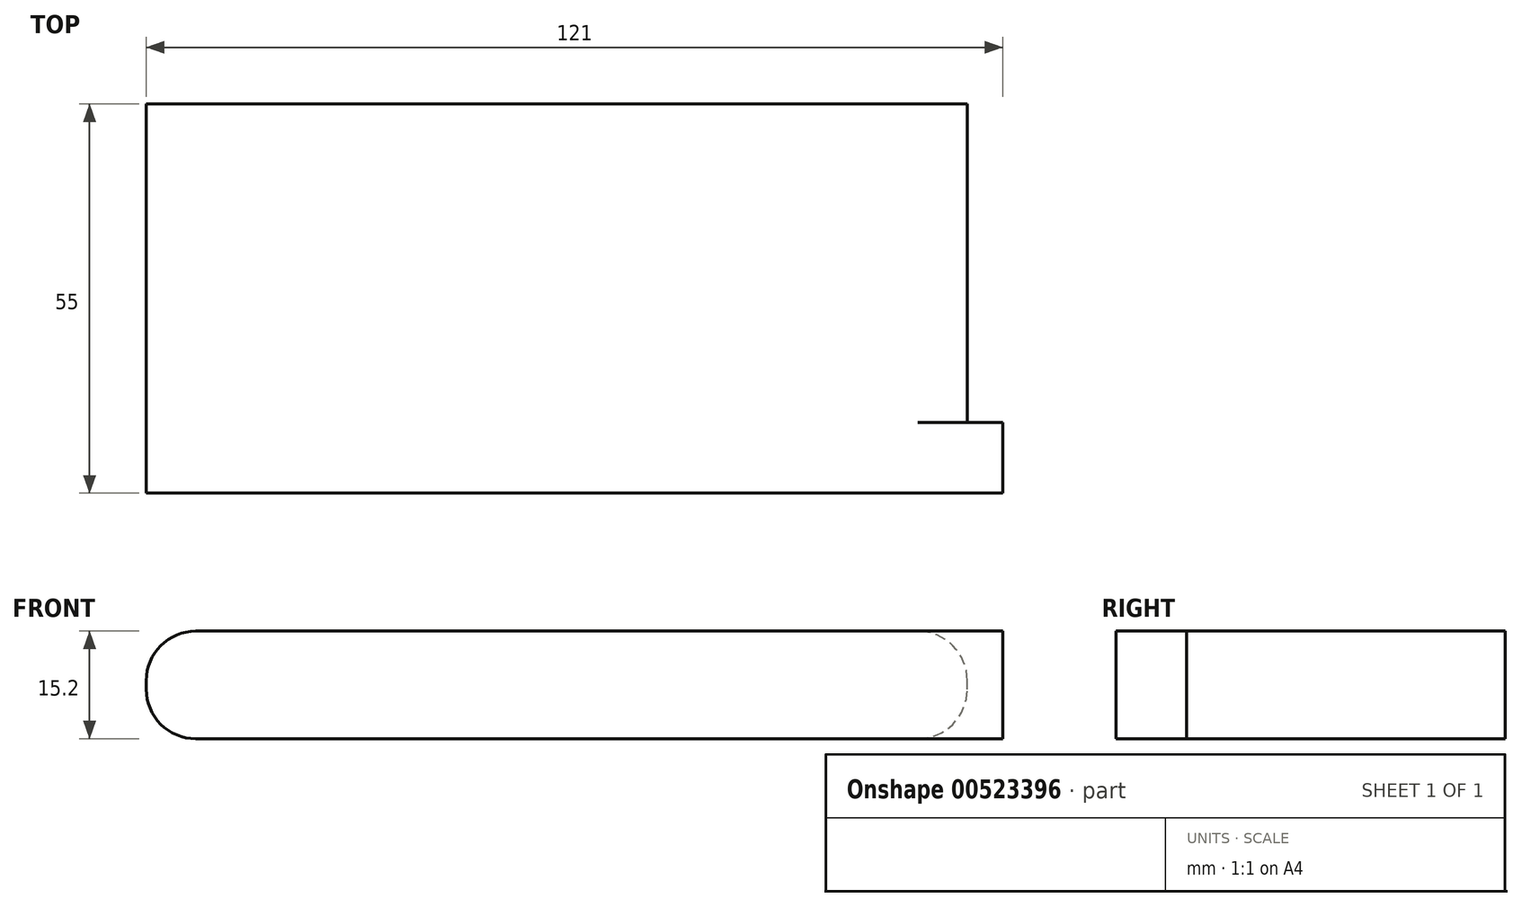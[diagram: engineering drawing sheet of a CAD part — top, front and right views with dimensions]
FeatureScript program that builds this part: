
annotation { "Feature Type Name" : "Feature", "Feature Type Description" : "" }
export const myFeature = defineFeature(function(context is Context, id is Id, definition is map)
    precondition{}
    {
        {
            var Q0;
            Q0=qCreatedBy(makeId("Top.planeOp"),FACE);
            var sketch = newSketch(context, id + "F0", { "sketchPlane" : qUnion([Q0])});
            skLineSegment(sketch, "E0.bottom", {"start": v(58, 27.5) * mm, "end": v(-58, 27.5) * mm});
            skLineSegment(sketch, "E0.top", {"start": v(58, -27.5) * mm, "end": v(-58, -27.5) * mm});
            skLineSegment(sketch, "E0.left", {"start": v(58, 27.5) * mm, "end": v(58, -27.5) * mm});
            skLineSegment(sketch, "E0.right", {"start": v(-58, 27.5) * mm, "end": v(-58, -27.5) * mm});
            skPoint(sketch, "E0.middle", {"position": v(0, 0) * mm});
            skSolve(sketch);
        }
        {
            var Q0;
            Q0=makeQuery(id+"F0.imprint","IMPRINT",FACE,{"disambiguationData":[TD([[makeQuery(id+"F0.imprint","IMPRINT",EDGE,{"derivedFrom":sQuery(id+"F0.wireOp",EDGE,"E0.bottom")}),1.0]])]});
            extrude(context, id + "F1", {"entities" : qUnion([Q0]), "depth" : 15.2 * mm, "offsetDistance" : 25 * mm});
        }
        {
            var Q0;
            Q0=makeQuery(id+"F1.opExtrude","CAP_EDGE",EDGE,{"disambiguationData":[OSD([sQuery(id+"F0.wireOp",EDGE,"E0.left")])],"isStart":false});
            var Q1;
            Q1=makeQuery(id+"F1.opExtrude","CAP_EDGE",EDGE,{"disambiguationData":[OSD([sQuery(id+"F0.wireOp",EDGE,"E0.left")])],"isStart":true});
            var Q2;
            Q2=makeQuery(id+"F1.opExtrude","CAP_EDGE",EDGE,{"disambiguationData":[OSD([sQuery(id+"F0.wireOp",EDGE,"E0.right")])],"isStart":false});
            var Q3;
            Q3=makeQuery(id+"F1.opExtrude","CAP_EDGE",EDGE,{"disambiguationData":[OSD([sQuery(id+"F0.wireOp",EDGE,"E0.right")])],"isStart":true});
            fillet(context, id + "F2", {"entities" : qUnion([Q0, Q1, Q2, Q3]), "radius" : 7 * mm, "tangentPropagation" : true, "allowEdgeOverflow" : false});
        }
        {
            var Q0;
            Q0=makeQuery(id+"F1.opExtrude","SWEPT_FACE",FACE,{"disambiguationData":[OSD([sQuery(id+"F0.wireOp",EDGE,"E0.left")])]});
            var sketch = newSketch(context, id + "F3", { "sketchPlane" : qUnion([Q0])});
            skLineSegment(sketch, "E1.bottom", {"start": v(-17.5, 15.2) * mm, "end": v(-27.5, 15.2) * mm});
            skLineSegment(sketch, "E1.top", {"start": v(-17.5, 0) * mm, "end": v(-27.5, 0) * mm});
            skLineSegment(sketch, "E1.left", {"start": v(-17.5, 15.2) * mm, "end": v(-17.5, 0) * mm});
            skLineSegment(sketch, "E1.right", {"start": v(-27.5, 15.2) * mm, "end": v(-27.5, 0) * mm});
            skPoint(sketch, "E1.middle", {"position": v(-22.5, 7.6) * mm});
            skSolve(sketch);
        }
        {
            var Q0;
            Q0 = qSketchRegion(id + "F3", true);
            extrude(context, id + "F4", {"entities" : qUnion([Q0]), "operationType" : NewBodyOperationType.ADD, "depth" : 5 * mm, "offsetDistance" : 25 * mm, "hasSecondDirection" : true, "secondDirectionOppositeDirection" : true, "secondDirectionDepth" : 10 * mm});
        }
    });
